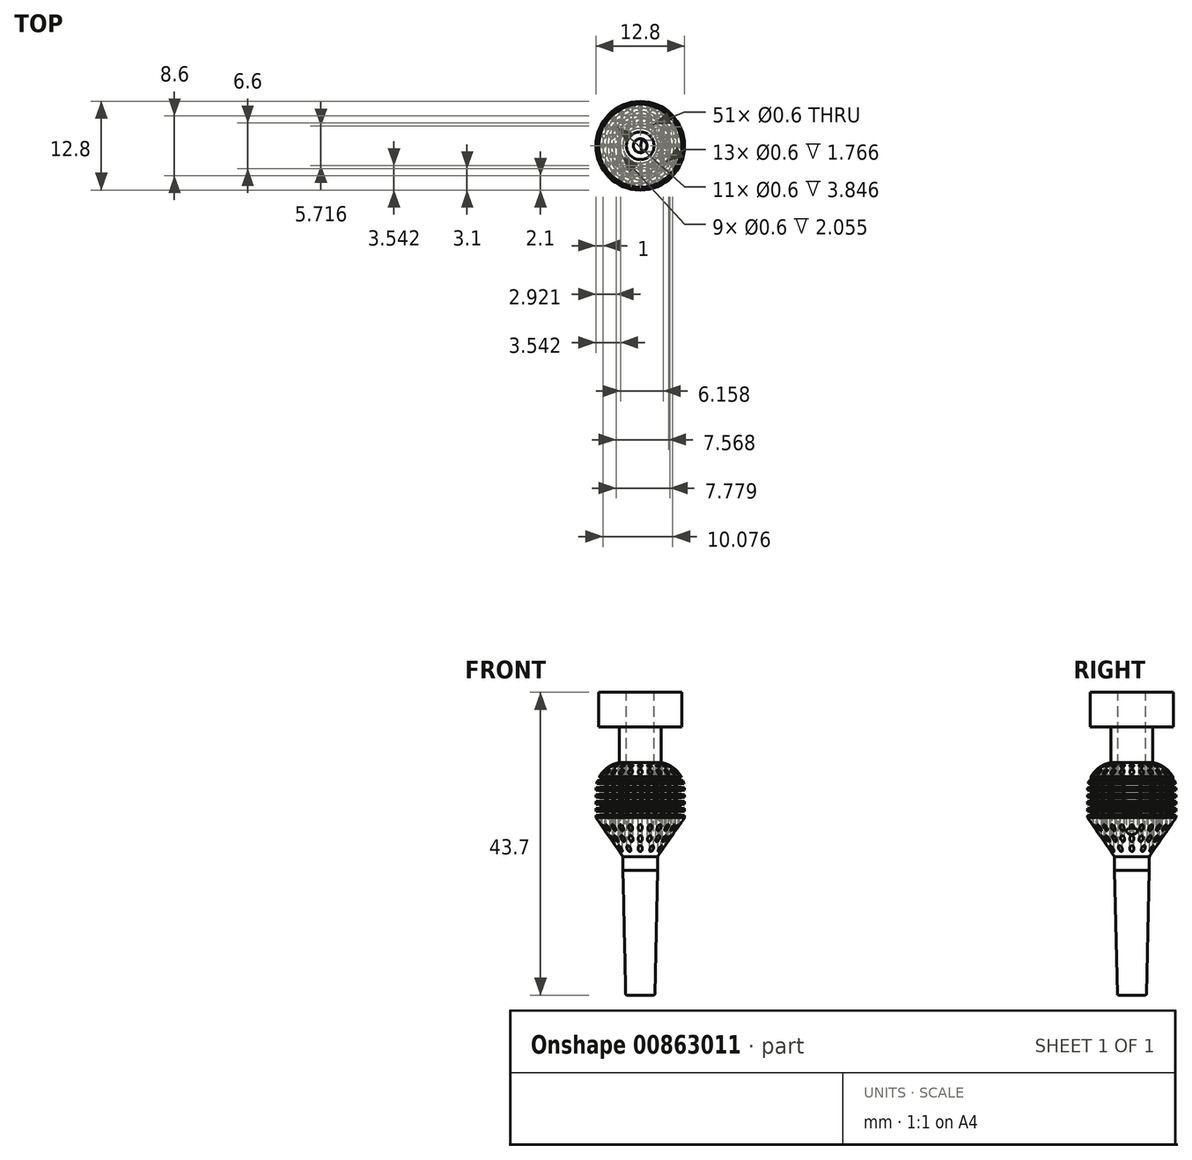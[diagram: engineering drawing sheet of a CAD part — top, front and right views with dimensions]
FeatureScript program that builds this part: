
annotation { "Feature Type Name" : "Feature", "Feature Type Description" : "" }
export const myFeature = defineFeature(function(context is Context, id is Id, definition is map)
    precondition{}
    {
        {
            var Q0;
            Q0=qCreatedBy(makeId("Front.planeOp"),FACE);
            var sketch = newSketch(context, id + "F0", { "sketchPlane" : qUnion([Q0])});
            skLineSegment(sketch, "E0", {"start": v(0, 0) * mm, "end": v(0, -20) * mm});
            skLineSegment(sketch, "E1", {"start": v(0, -20) * mm, "end": v(2.5, -20) * mm});
            skLineSegment(sketch, "E2", {"start": v(2.5, -20) * mm, "end": v(2.5, -0.32) * mm});
            skLineSegment(sketch, "E3", {"start": v(2.68, 0.26) * mm, "end": v(6.33, 5.48) * mm});
            skLineSegment(sketch, "E4", {"start": v(6.52, 6.05) * mm, "end": v(6.52, 9.73) * mm});
            skArc(sketch, "E5", {"start": v(6.52, 9.73) * mm, "mid": v(5.34, 12.57) * mm, "end": v(2.5, 13.73) * mm});
            skLineSegment(sketch, "E6", {"start": v(2.5, 13.73) * mm, "end": v(0, 13.72) * mm});
            skLineSegment(sketch, "E7", {"start": v(0, 0) * mm, "end": v(0, 13.72) * mm});
            skPoint(sketch, "E8.visualSharp", {"position": v(2.5, 0) * mm});
            skArc(sketch, "E8.filletArc", {"start": v(2.68, 0.26) * mm, "mid": v(2.55, -0.01) * mm, "end": v(2.5, -0.32) * mm});
            skPoint(sketch, "E9.visualSharp", {"position": v(6.52, 5.73) * mm});
            skArc(sketch, "E9.filletArc", {"start": v(6.33, 5.48) * mm, "mid": v(6.47, 5.75) * mm, "end": v(6.52, 6.05) * mm});
            skSolve(sketch);
        }
        {
            var Q0;
            Q0=makeQuery(id+"F0.imprint","IMPRINT",FACE,{"disambiguationData":[TD([[makeQuery(id+"F0.imprint","IMPRINT",EDGE,{"derivedFrom":sQuery(id+"F0.wireOp",EDGE,"E0")}),1.0]])]});
            var Q1;
            Q1=sQuery(id+"F0.wireOp",EDGE,"E7");
            revolve(context, id + "F1", {"surfaceOperationType" : NewSurfaceOperationType.NEW, "entities" : qUnion([Q0]), "axis" : qUnion([Q1]), "revolveType" : RevolveType.FULL});
        }
        {
            var Q0;
            Q0=qCreatedBy(makeId("Front.planeOp"),FACE);
            var sketch = newSketch(context, id + "F2", { "sketchPlane" : qUnion([Q0])});
            skLineSegment(sketch, "E10.bottom", {"start": v(2.5, 11.5) * mm, "end": v(7.5, 11.5) * mm});
            skLineSegment(sketch, "E10.top", {"start": v(2.5, 11) * mm, "end": v(7.5, 11) * mm});
            skLineSegment(sketch, "E10.left", {"start": v(2.5, 11.5) * mm, "end": v(2.5, 11) * mm});
            skLineSegment(sketch, "E10.right", {"start": v(7.5, 11.5) * mm, "end": v(7.5, 11) * mm});
            skLineSegment(sketch, "E11.0.1.0", {"start": v(2.5, 10) * mm, "end": v(7.5, 10) * mm});
            skLineSegment(sketch, "E11.0.1.1", {"start": v(2.5, 10.5) * mm, "end": v(7.5, 10.5) * mm});
            skLineSegment(sketch, "E11.0.1.2", {"start": v(2.5, 10.5) * mm, "end": v(2.5, 10) * mm});
            skLineSegment(sketch, "E11.0.1.3", {"start": v(7.5, 10.5) * mm, "end": v(7.5, 10) * mm});
            skLineSegment(sketch, "E11.0.2.0", {"start": v(2.5, 9) * mm, "end": v(7.5, 9) * mm});
            skLineSegment(sketch, "E11.0.2.1", {"start": v(2.5, 9.5) * mm, "end": v(7.5, 9.5) * mm});
            skLineSegment(sketch, "E11.0.2.2", {"start": v(2.5, 9.5) * mm, "end": v(2.5, 9) * mm});
            skLineSegment(sketch, "E11.0.2.3", {"start": v(7.5, 9.5) * mm, "end": v(7.5, 9) * mm});
            skLineSegment(sketch, "E11.0.3.0", {"start": v(2.5, 8) * mm, "end": v(7.5, 8) * mm});
            skLineSegment(sketch, "E11.0.3.1", {"start": v(2.5, 8.5) * mm, "end": v(7.5, 8.5) * mm});
            skLineSegment(sketch, "E11.0.3.2", {"start": v(2.5, 8.5) * mm, "end": v(2.5, 8) * mm});
            skLineSegment(sketch, "E11.0.3.3", {"start": v(7.5, 8.5) * mm, "end": v(7.5, 8) * mm});
            skLineSegment(sketch, "E11.direction1", {"start": v(2.5, 11) * mm, "end": v(27.5, 11) * mm, "construction": true});
            skLineSegment(sketch, "E11.direction2", {"start": v(2.5, 11) * mm, "end": v(2.5, 10) * mm, "construction": true});
            skLineSegment(sketch, "E12.0.0.4", {"start": v(2.5, 7) * mm, "end": v(7.5, 7) * mm});
            skLineSegment(sketch, "E12.3.0.4", {"start": v(2.5, 7.5) * mm, "end": v(7.5, 7.5) * mm});
            skLineSegment(sketch, "E12.6.0.4", {"start": v(2.5, 7.5) * mm, "end": v(2.5, 7) * mm});
            skLineSegment(sketch, "E12.9.0.4", {"start": v(7.5, 7.5) * mm, "end": v(7.5, 7) * mm});
            skLineSegment(sketch, "E13.0.0.5", {"start": v(2.5, 6) * mm, "end": v(7.5, 6) * mm});
            skLineSegment(sketch, "E13.3.0.5", {"start": v(2.5, 6.5) * mm, "end": v(7.5, 6.5) * mm});
            skLineSegment(sketch, "E13.6.0.5", {"start": v(2.5, 6.5) * mm, "end": v(2.5, 6) * mm});
            skLineSegment(sketch, "E13.9.0.5", {"start": v(7.5, 6.5) * mm, "end": v(7.5, 6) * mm});
            skSolve(sketch);
        }
        {
            var Q0;
            Q0=qCreatedBy(makeId("Front.planeOp"),FACE);
            var sketch = newSketch(context, id + "F3", { "sketchPlane" : qUnion([Q0])});
            skLineSegment(sketch, "E14", {"start": v(0, 35.11) * mm, "end": v(0, -39.83) * mm, "construction": true});
            skSolve(sketch);
        }
        {
            var Q0;
            Q0=qSketchRegion(id+"F2",true);
            var Q1;
            Q1=sQuery(id+"F3.wireOp",EDGE,"E14");
            var Q2;
            Q2=qConstructionFilter(qBodyType(qCreatedBy(id+"F2",EDGE),BodyType.WIRE),ConstructionObject.NO);
            var Q3;
            Q3=sQuery(id+"F3.wireOp",EDGE,"E14");
            revolve(context, id + "F4", {"operationType" : NewBodyOperationType.REMOVE, "surfaceOperationType" : NewSurfaceOperationType.NEW, "entities" : qUnion([Q0]), "surfaceEntities" : qUnion([Q1, Q2]), "axis" : qUnion([Q3]), "revolveType" : RevolveType.FULL, "oppositeDirection" : true});
        }
        {
            var Q0;
            Q0=qCreatedBy(makeId("Top.planeOp"),FACE);
            cPlane(context, id + "F5", {"entities" : qUnion([Q0]), "cplaneType" : CPlaneType.OFFSET, "offset" : 13.7 * mm, "width" : 150 * mm, "height" : 150 * mm});
        }
        {
            var Q0;
            Q0=qCreatedBy(id+"F5.planeOp",FACE);
            var sketch = newSketch(context, id + "F6", { "sketchPlane" : qUnion([Q0])});
            skCircle(sketch, "E15", {"center": v(0, 3.3) * mm, "radius": 0.3 * mm});
            skCircle(sketch, "E16.1.0", {"center": v(-1.65, 2.86) * mm, "radius": 0.3 * mm});
            skCircle(sketch, "E16.2.0", {"center": v(-2.86, 1.65) * mm, "radius": 0.3 * mm});
            skCircle(sketch, "E16.3.0", {"center": v(-3.3, 0) * mm, "radius": 0.3 * mm});
            skCircle(sketch, "E16.4.0", {"center": v(-2.86, -1.65) * mm, "radius": 0.3 * mm});
            skCircle(sketch, "E16.5.0", {"center": v(-1.65, -2.86) * mm, "radius": 0.3 * mm});
            skCircle(sketch, "E16.6.0", {"center": v(0, -3.3) * mm, "radius": 0.3 * mm});
            skCircle(sketch, "E16.7.0", {"center": v(1.65, -2.86) * mm, "radius": 0.3 * mm});
            skCircle(sketch, "E16.8.0", {"center": v(2.86, -1.65) * mm, "radius": 0.3 * mm});
            skCircle(sketch, "E16.9.0", {"center": v(3.3, 0) * mm, "radius": 0.3 * mm});
            skPoint(sketch, "E16.center", {"position": v(0, 0) * mm});
            skCircle(sketch, "E17", {"center": v(0, 4.3) * mm, "radius": 0.3 * mm});
            skCircle(sketch, "E18.1.0", {"center": v(-1.33, 4.09) * mm, "radius": 0.3 * mm});
            skCircle(sketch, "E18.2.0", {"center": v(-2.53, 3.48) * mm, "radius": 0.3 * mm});
            skCircle(sketch, "E18.3.0", {"center": v(-3.48, 2.53) * mm, "radius": 0.3 * mm});
            skCircle(sketch, "E18.4.0", {"center": v(-4.09, 1.33) * mm, "radius": 0.3 * mm});
            skCircle(sketch, "E18.5.0", {"center": v(-4.3, 0) * mm, "radius": 0.3 * mm});
            skCircle(sketch, "E18.6.0", {"center": v(-4.09, -1.33) * mm, "radius": 0.3 * mm});
            skCircle(sketch, "E18.7.0", {"center": v(-3.48, -2.53) * mm, "radius": 0.3 * mm});
            skCircle(sketch, "E18.8.0", {"center": v(-2.53, -3.48) * mm, "radius": 0.3 * mm});
            skCircle(sketch, "E18.9.0", {"center": v(-1.33, -4.09) * mm, "radius": 0.3 * mm});
            skCircle(sketch, "E18.10.0", {"center": v(0, -4.3) * mm, "radius": 0.3 * mm});
            skCircle(sketch, "E18.11.0", {"center": v(1.33, -4.09) * mm, "radius": 0.3 * mm});
            skCircle(sketch, "E18.12.0", {"center": v(2.53, -3.48) * mm, "radius": 0.3 * mm});
            skCircle(sketch, "E18.13.0", {"center": v(3.48, -2.53) * mm, "radius": 0.3 * mm});
            skCircle(sketch, "E18.14.0", {"center": v(4.09, -1.33) * mm, "radius": 0.3 * mm});
            skCircle(sketch, "E18.15.0", {"center": v(4.3, 0) * mm, "radius": 0.3 * mm});
            skCircle(sketch, "E19", {"center": v(0, 5.4) * mm, "radius": 0.3 * mm});
            skCircle(sketch, "E20.1.0", {"center": v(-1.4, 5.22) * mm, "radius": 0.3 * mm});
            skCircle(sketch, "E20.2.0", {"center": v(-2.7, 4.68) * mm, "radius": 0.3 * mm});
            skCircle(sketch, "E20.3.0", {"center": v(-3.82, 3.82) * mm, "radius": 0.3 * mm});
            skCircle(sketch, "E20.4.0", {"center": v(-4.68, 2.7) * mm, "radius": 0.3 * mm});
            skCircle(sketch, "E20.5.0", {"center": v(-5.22, 1.4) * mm, "radius": 0.3 * mm});
            skCircle(sketch, "E20.6.0", {"center": v(-5.4, 0) * mm, "radius": 0.3 * mm});
            skCircle(sketch, "E20.7.0", {"center": v(-5.22, -1.4) * mm, "radius": 0.3 * mm});
            skCircle(sketch, "E20.8.0", {"center": v(-4.68, -2.7) * mm, "radius": 0.3 * mm});
            skCircle(sketch, "E20.9.0", {"center": v(-3.82, -3.82) * mm, "radius": 0.3 * mm});
            skCircle(sketch, "E20.10.0", {"center": v(-2.7, -4.68) * mm, "radius": 0.3 * mm});
            skCircle(sketch, "E20.11.0", {"center": v(-1.4, -5.22) * mm, "radius": 0.3 * mm});
            skCircle(sketch, "E20.12.0", {"center": v(0, -5.4) * mm, "radius": 0.3 * mm});
            skCircle(sketch, "E20.13.0", {"center": v(1.4, -5.22) * mm, "radius": 0.3 * mm});
            skCircle(sketch, "E20.14.0", {"center": v(2.7, -4.68) * mm, "radius": 0.3 * mm});
            skCircle(sketch, "E20.15.0", {"center": v(3.82, -3.82) * mm, "radius": 0.3 * mm});
            skCircle(sketch, "E20.16.0", {"center": v(4.68, -2.7) * mm, "radius": 0.3 * mm});
            skCircle(sketch, "E20.17.0", {"center": v(5.22, -1.4) * mm, "radius": 0.3 * mm});
            skCircle(sketch, "E20.18.0", {"center": v(5.4, 0) * mm, "radius": 0.3 * mm});
            skCircle(sketch, "E20.19.0", {"center": v(5.22, 1.4) * mm, "radius": 0.3 * mm});
            skCircle(sketch, "E21.1.10.0", {"center": v(2.86, 1.65) * mm, "radius": 0.3 * mm});
            skCircle(sketch, "E21.1.11.0", {"center": v(1.65, 2.86) * mm, "radius": 0.3 * mm});
            skCircle(sketch, "E22.1.16.0", {"center": v(4.09, 1.33) * mm, "radius": 0.3 * mm});
            skCircle(sketch, "E22.1.17.0", {"center": v(3.48, 2.53) * mm, "radius": 0.3 * mm});
            skCircle(sketch, "E22.1.18.0", {"center": v(2.53, 3.48) * mm, "radius": 0.3 * mm});
            skCircle(sketch, "E22.1.19.0", {"center": v(1.33, 4.09) * mm, "radius": 0.3 * mm});
            skCircle(sketch, "E23.1.20.0", {"center": v(4.68, 2.7) * mm, "radius": 0.3 * mm});
            skCircle(sketch, "E23.1.21.0", {"center": v(3.82, 3.82) * mm, "radius": 0.3 * mm});
            skCircle(sketch, "E23.1.22.0", {"center": v(2.7, 4.68) * mm, "radius": 0.3 * mm});
            skCircle(sketch, "E23.1.23.0", {"center": v(1.4, 5.22) * mm, "radius": 0.3 * mm});
            skSolve(sketch);
        }
        {
            var Q0;
            Q0=qSketchRegion(id+"F6",true);
            extrude(context, id + "F7", {"entities" : qUnion([Q0]), "operationType" : NewBodyOperationType.REMOVE, "oppositeDirection" : true, "depth" : 16.5 * mm, "offsetDistance" : 25 * mm});
        }
        {
            var Q0;
            Q0=qCreatedBy(makeId("Front.planeOp"),FACE);
            cPlane(context, id + "F8", {"entities" : qUnion([Q0]), "cplaneType" : CPlaneType.OFFSET, "offset" : 7 * mm, "width" : 150 * mm, "height" : 150 * mm});
        }
        {
            var Q0;
            Q0=qCreatedBy(id+"F8.planeOp",FACE);
            var sketch = newSketch(context, id + "F9", { "sketchPlane" : qUnion([Q0])});
            skLineSegment(sketch, "E24.bottom", {"start": v(-4.75, 11.8) * mm, "end": v(-5, 11.8) * mm});
            skLineSegment(sketch, "E24.top", {"start": v(-4.75, 5.8) * mm, "end": v(-5, 5.8) * mm});
            skLineSegment(sketch, "E24.left", {"start": v(-4.75, 11.8) * mm, "end": v(-4.75, 5.8) * mm});
            skLineSegment(sketch, "E24.right", {"start": v(-5, 11.8) * mm, "end": v(-5, 5.8) * mm});
            skLineSegment(sketch, "E25.1.0.0", {"start": v(-4, 11.8) * mm, "end": v(-4, 5.8) * mm});
            skLineSegment(sketch, "E25.1.0.1", {"start": v(-3.75, 11.8) * mm, "end": v(-3.75, 5.8) * mm});
            skLineSegment(sketch, "E25.1.0.2", {"start": v(-3.75, 5.8) * mm, "end": v(-4, 5.8) * mm});
            skLineSegment(sketch, "E25.1.0.3", {"start": v(-3.75, 11.8) * mm, "end": v(-4, 11.8) * mm});
            skLineSegment(sketch, "E25.2.0.0", {"start": v(-3, 11.8) * mm, "end": v(-3, 5.8) * mm});
            skLineSegment(sketch, "E25.2.0.1", {"start": v(-2.75, 11.8) * mm, "end": v(-2.75, 5.8) * mm});
            skLineSegment(sketch, "E25.2.0.2", {"start": v(-2.75, 5.8) * mm, "end": v(-3, 5.8) * mm});
            skLineSegment(sketch, "E25.2.0.3", {"start": v(-2.75, 11.8) * mm, "end": v(-3, 11.8) * mm});
            skLineSegment(sketch, "E25.3.0.0", {"start": v(-2, 11.8) * mm, "end": v(-2, 5.8) * mm});
            skLineSegment(sketch, "E25.3.0.1", {"start": v(-1.75, 11.8) * mm, "end": v(-1.75, 5.8) * mm});
            skLineSegment(sketch, "E25.3.0.2", {"start": v(-1.75, 5.8) * mm, "end": v(-2, 5.8) * mm});
            skLineSegment(sketch, "E25.3.0.3", {"start": v(-1.75, 11.8) * mm, "end": v(-2, 11.8) * mm});
            skLineSegment(sketch, "E25.4.0.0", {"start": v(-1, 11.8) * mm, "end": v(-1, 5.8) * mm});
            skLineSegment(sketch, "E25.4.0.1", {"start": v(-0.75, 11.8) * mm, "end": v(-0.75, 5.8) * mm});
            skLineSegment(sketch, "E25.4.0.2", {"start": v(-0.75, 5.8) * mm, "end": v(-1, 5.8) * mm});
            skLineSegment(sketch, "E25.4.0.3", {"start": v(-0.75, 11.8) * mm, "end": v(-1, 11.8) * mm});
            skLineSegment(sketch, "E25.5.0.0", {"start": v(0, 11.8) * mm, "end": v(0, 5.8) * mm});
            skLineSegment(sketch, "E25.5.0.1", {"start": v(0.25, 11.8) * mm, "end": v(0.25, 5.8) * mm});
            skLineSegment(sketch, "E25.5.0.2", {"start": v(0.25, 5.8) * mm, "end": v(0, 5.8) * mm});
            skLineSegment(sketch, "E25.5.0.3", {"start": v(0.25, 11.8) * mm, "end": v(0, 11.8) * mm});
            skLineSegment(sketch, "E25.6.0.0", {"start": v(1, 11.8) * mm, "end": v(1, 5.8) * mm});
            skLineSegment(sketch, "E25.6.0.1", {"start": v(1.25, 11.8) * mm, "end": v(1.25, 5.8) * mm});
            skLineSegment(sketch, "E25.6.0.2", {"start": v(1.25, 5.8) * mm, "end": v(1, 5.8) * mm});
            skLineSegment(sketch, "E25.6.0.3", {"start": v(1.25, 11.8) * mm, "end": v(1, 11.8) * mm});
            skLineSegment(sketch, "E25.7.0.0", {"start": v(2, 11.8) * mm, "end": v(2, 5.8) * mm});
            skLineSegment(sketch, "E25.7.0.1", {"start": v(2.25, 11.8) * mm, "end": v(2.25, 5.8) * mm});
            skLineSegment(sketch, "E25.7.0.2", {"start": v(2.25, 5.8) * mm, "end": v(2, 5.8) * mm});
            skLineSegment(sketch, "E25.7.0.3", {"start": v(2.25, 11.8) * mm, "end": v(2, 11.8) * mm});
            skLineSegment(sketch, "E25.8.0.0", {"start": v(3, 11.8) * mm, "end": v(3, 5.8) * mm});
            skLineSegment(sketch, "E25.8.0.1", {"start": v(3.25, 11.8) * mm, "end": v(3.25, 5.8) * mm});
            skLineSegment(sketch, "E25.8.0.2", {"start": v(3.25, 5.8) * mm, "end": v(3, 5.8) * mm});
            skLineSegment(sketch, "E25.8.0.3", {"start": v(3.25, 11.8) * mm, "end": v(3, 11.8) * mm});
            skLineSegment(sketch, "E25.9.0.0", {"start": v(4, 11.8) * mm, "end": v(4, 5.8) * mm});
            skLineSegment(sketch, "E25.9.0.1", {"start": v(4.25, 11.8) * mm, "end": v(4.25, 5.8) * mm});
            skLineSegment(sketch, "E25.9.0.2", {"start": v(4.25, 5.8) * mm, "end": v(4, 5.8) * mm});
            skLineSegment(sketch, "E25.9.0.3", {"start": v(4.25, 11.8) * mm, "end": v(4, 11.8) * mm});
            skLineSegment(sketch, "E25.10.0.0", {"start": v(5, 11.8) * mm, "end": v(5, 5.8) * mm});
            skLineSegment(sketch, "E25.10.0.1", {"start": v(5.25, 11.8) * mm, "end": v(5.25, 5.8) * mm});
            skLineSegment(sketch, "E25.10.0.2", {"start": v(5.25, 5.8) * mm, "end": v(5, 5.8) * mm});
            skLineSegment(sketch, "E25.10.0.3", {"start": v(5.25, 11.8) * mm, "end": v(5, 11.8) * mm});
            skLineSegment(sketch, "E25.direction1", {"start": v(-5, 5.8) * mm, "end": v(-4, 5.8) * mm, "construction": true});
            skLineSegment(sketch, "E25.direction2", {"start": v(-5, 5.8) * mm, "end": v(-5, 3.8) * mm, "construction": true});
            skSolve(sketch);
        }
        {
            var Q0;
            Q0=qSketchRegion(id+"F9",true);
            extrude(context, id + "F10", {"entities" : qUnion([Q0]), "operationType" : NewBodyOperationType.ADD, "oppositeDirection" : true, "depth" : 14.3 * mm, "offsetDistance" : 25 * mm});
        }
        {
            var Q0;
            Q0=qCreatedBy(makeId("Right.planeOp"),FACE);
            var sketch = newSketch(context, id + "F11", { "sketchPlane" : qUnion([Q0])});
            skLineSegment(sketch, "E26", {"start": v(-2.5, 0) * mm, "end": v(-6.4, 5.6) * mm});
            skLineSegment(sketch, "E27", {"start": v(-6.4, 5.6) * mm, "end": v(-6.4, 9.6) * mm});
            skArc(sketch, "E28", {"start": v(-2.4, 13.6) * mm, "mid": v(-5.23, 12.43) * mm, "end": v(-6.4, 9.6) * mm});
            skLineSegment(sketch, "E29", {"start": v(-2.4, 13.6) * mm, "end": v(-2.4, 16) * mm});
            skLineSegment(sketch, "E30", {"start": v(-2.4, 16) * mm, "end": v(-14.4, 16) * mm});
            skLineSegment(sketch, "E31", {"start": v(-14.4, 16) * mm, "end": v(-14.5, 0) * mm});
            skLineSegment(sketch, "E32", {"start": v(-14.5, 0) * mm, "end": v(-2.5, 0) * mm});
            skSolve(sketch);
        }
        {
            var Q0;
            Q0=qCreatedBy(makeId("Right.planeOp"),FACE);
            var sketch = newSketch(context, id + "F12", { "sketchPlane" : qUnion([Q0])});
            skLineSegment(sketch, "E33", {"start": v(0, -8.71) * mm, "end": v(0, 18.1) * mm, "construction": true});
            skSolve(sketch);
        }
        {
            var Q0;
            Q0=makeQuery(id+"F11.imprint","IMPRINT",FACE,{"disambiguationData":[TD([[makeQuery(id+"F11.imprint","IMPRINT",EDGE,{"derivedFrom":sQuery(id+"F11.wireOp",EDGE,"E26")}),1.0]])]});
            var Q1;
            Q1=sQuery(id+"F12.wireOp",EDGE,"E33");
            var Q2;
            Q2=sQuery(id+"F12.wireOp",EDGE,"E33");
            revolve(context, id + "F13", {"operationType" : NewBodyOperationType.REMOVE, "surfaceOperationType" : NewSurfaceOperationType.NEW, "entities" : qUnion([Q0]), "surfaceEntities" : qUnion([Q1]), "axis" : qUnion([Q2]), "revolveType" : RevolveType.FULL, "oppositeDirection" : true});
        }
        {
            var Q0;
            Q0=qCreatedBy(id+"F5.planeOp",FACE);
            var sketch = newSketch(context, id + "F14", { "sketchPlane" : qUnion([Q0])});
            skCircle(sketch, "E34", {"center": v(0, 0) * mm, "radius": 3 * mm});
            skSolve(sketch);
        }
        {
            var Q0;
            Q0=qSketchRegion(id+"F14",true);
            extrude(context, id + "F15", {"entities" : qUnion([Q0]), "operationType" : NewBodyOperationType.ADD, "depth" : 10 * mm, "offsetDistance" : 25 * mm, "hasSecondDirection" : true, "secondDirectionOppositeDirection" : true, "secondDirectionDepth" : 1 * mm});
        }
        {
            var Q0;
            Q0=qCreatedBy(makeId("Right.planeOp"),FACE);
            var sketch = newSketch(context, id + "F16", { "sketchPlane" : qUnion([Q0])});
            skLineSegment(sketch, "E35.bottom", {"start": v(-6.4, 5.95) * mm, "end": v(-5.9, 5.95) * mm});
            skLineSegment(sketch, "E35.top", {"start": v(-6.4, 6.55) * mm, "end": v(-5.9, 6.55) * mm});
            skLineSegment(sketch, "E35.left", {"start": v(-6.4, 5.95) * mm, "end": v(-6.4, 6.55) * mm});
            skLineSegment(sketch, "E35.right", {"start": v(-5.9, 5.95) * mm, "end": v(-5.9, 6.55) * mm});
            skLineSegment(sketch, "E36.0.1.0", {"start": v(-6.4, 7.55) * mm, "end": v(-5.9, 7.55) * mm});
            skLineSegment(sketch, "E36.0.1.1", {"start": v(-5.9, 6.95) * mm, "end": v(-5.9, 7.55) * mm});
            skLineSegment(sketch, "E36.0.1.2", {"start": v(-6.4, 6.95) * mm, "end": v(-6.4, 7.55) * mm});
            skLineSegment(sketch, "E36.0.1.3", {"start": v(-6.4, 6.95) * mm, "end": v(-5.9, 6.95) * mm});
            skLineSegment(sketch, "E36.0.2.0", {"start": v(-6.4, 8.55) * mm, "end": v(-5.9, 8.55) * mm});
            skLineSegment(sketch, "E36.0.2.1", {"start": v(-5.9, 7.95) * mm, "end": v(-5.9, 8.55) * mm});
            skLineSegment(sketch, "E36.0.2.2", {"start": v(-6.4, 7.95) * mm, "end": v(-6.4, 8.55) * mm});
            skLineSegment(sketch, "E36.0.2.3", {"start": v(-6.4, 7.95) * mm, "end": v(-5.9, 7.95) * mm});
            skLineSegment(sketch, "E36.0.3.0", {"start": v(-6.4, 9.55) * mm, "end": v(-5.9, 9.55) * mm});
            skLineSegment(sketch, "E36.0.3.1", {"start": v(-5.9, 8.95) * mm, "end": v(-5.9, 9.55) * mm});
            skLineSegment(sketch, "E36.0.3.2", {"start": v(-6.4, 8.95) * mm, "end": v(-6.4, 9.55) * mm});
            skLineSegment(sketch, "E36.0.3.3", {"start": v(-6.4, 8.95) * mm, "end": v(-5.9, 8.95) * mm});
            skLineSegment(sketch, "E36.0.4.0", {"start": v(-6.4, 10.55) * mm, "end": v(-5.9, 10.55) * mm});
            skLineSegment(sketch, "E36.0.4.1", {"start": v(-5.9, 9.95) * mm, "end": v(-5.9, 10.55) * mm});
            skLineSegment(sketch, "E36.0.4.2", {"start": v(-6.4, 9.95) * mm, "end": v(-6.4, 10.55) * mm});
            skLineSegment(sketch, "E36.0.4.3", {"start": v(-6.4, 9.95) * mm, "end": v(-5.9, 9.95) * mm});
            skLineSegment(sketch, "E36.0.5.0", {"start": v(-6.4, 11.55) * mm, "end": v(-5.9, 11.55) * mm});
            skLineSegment(sketch, "E36.0.5.1", {"start": v(-5.9, 10.95) * mm, "end": v(-5.9, 11.55) * mm});
            skLineSegment(sketch, "E36.0.5.2", {"start": v(-6.4, 10.95) * mm, "end": v(-6.4, 11.55) * mm});
            skLineSegment(sketch, "E36.0.5.3", {"start": v(-6.4, 10.95) * mm, "end": v(-5.9, 10.95) * mm});
            skLineSegment(sketch, "E36.1.0.0", {"start": v(-5.4, 6.55) * mm, "end": v(-4.9, 6.55) * mm});
            skLineSegment(sketch, "E36.1.0.1", {"start": v(-4.9, 5.95) * mm, "end": v(-4.9, 6.55) * mm});
            skLineSegment(sketch, "E36.1.0.2", {"start": v(-5.4, 5.95) * mm, "end": v(-5.4, 6.55) * mm});
            skLineSegment(sketch, "E36.1.0.3", {"start": v(-5.4, 5.95) * mm, "end": v(-4.9, 5.95) * mm});
            skLineSegment(sketch, "E36.1.1.0", {"start": v(-5.4, 7.55) * mm, "end": v(-4.9, 7.55) * mm});
            skLineSegment(sketch, "E36.1.1.1", {"start": v(-4.9, 6.95) * mm, "end": v(-4.9, 7.55) * mm});
            skLineSegment(sketch, "E36.1.1.2", {"start": v(-5.4, 6.95) * mm, "end": v(-5.4, 7.55) * mm});
            skLineSegment(sketch, "E36.1.1.3", {"start": v(-5.4, 6.95) * mm, "end": v(-4.9, 6.95) * mm});
            skLineSegment(sketch, "E36.1.2.0", {"start": v(-5.4, 8.55) * mm, "end": v(-4.9, 8.55) * mm});
            skLineSegment(sketch, "E36.1.2.1", {"start": v(-4.9, 7.95) * mm, "end": v(-4.9, 8.55) * mm});
            skLineSegment(sketch, "E36.1.2.2", {"start": v(-5.4, 7.95) * mm, "end": v(-5.4, 8.55) * mm});
            skLineSegment(sketch, "E36.1.2.3", {"start": v(-5.4, 7.95) * mm, "end": v(-4.9, 7.95) * mm});
            skLineSegment(sketch, "E36.1.3.0", {"start": v(-5.4, 9.55) * mm, "end": v(-4.9, 9.55) * mm});
            skLineSegment(sketch, "E36.1.3.1", {"start": v(-4.9, 8.95) * mm, "end": v(-4.9, 9.55) * mm});
            skLineSegment(sketch, "E36.1.3.2", {"start": v(-5.4, 8.95) * mm, "end": v(-5.4, 9.55) * mm});
            skLineSegment(sketch, "E36.1.3.3", {"start": v(-5.4, 8.95) * mm, "end": v(-4.9, 8.95) * mm});
            skLineSegment(sketch, "E36.1.4.0", {"start": v(-5.4, 10.55) * mm, "end": v(-4.9, 10.55) * mm});
            skLineSegment(sketch, "E36.1.4.1", {"start": v(-4.9, 9.95) * mm, "end": v(-4.9, 10.55) * mm});
            skLineSegment(sketch, "E36.1.4.2", {"start": v(-5.4, 9.95) * mm, "end": v(-5.4, 10.55) * mm});
            skLineSegment(sketch, "E36.1.4.3", {"start": v(-5.4, 9.95) * mm, "end": v(-4.9, 9.95) * mm});
            skLineSegment(sketch, "E36.1.5.0", {"start": v(-5.4, 11.55) * mm, "end": v(-4.9, 11.55) * mm});
            skLineSegment(sketch, "E36.1.5.1", {"start": v(-4.9, 10.95) * mm, "end": v(-4.9, 11.55) * mm});
            skLineSegment(sketch, "E36.1.5.2", {"start": v(-5.4, 10.95) * mm, "end": v(-5.4, 11.55) * mm});
            skLineSegment(sketch, "E36.1.5.3", {"start": v(-5.4, 10.95) * mm, "end": v(-4.9, 10.95) * mm});
            skLineSegment(sketch, "E36.2.0.0", {"start": v(-4.4, 6.55) * mm, "end": v(-3.9, 6.55) * mm});
            skLineSegment(sketch, "E36.2.0.1", {"start": v(-3.9, 5.95) * mm, "end": v(-3.9, 6.55) * mm});
            skLineSegment(sketch, "E36.2.0.2", {"start": v(-4.4, 5.95) * mm, "end": v(-4.4, 6.55) * mm});
            skLineSegment(sketch, "E36.2.0.3", {"start": v(-4.4, 5.95) * mm, "end": v(-3.9, 5.95) * mm});
            skLineSegment(sketch, "E36.2.1.0", {"start": v(-4.4, 7.55) * mm, "end": v(-3.9, 7.55) * mm});
            skLineSegment(sketch, "E36.2.1.1", {"start": v(-3.9, 6.95) * mm, "end": v(-3.9, 7.55) * mm});
            skLineSegment(sketch, "E36.2.1.2", {"start": v(-4.4, 6.95) * mm, "end": v(-4.4, 7.55) * mm});
            skLineSegment(sketch, "E36.2.1.3", {"start": v(-4.4, 6.95) * mm, "end": v(-3.9, 6.95) * mm});
            skLineSegment(sketch, "E36.2.2.0", {"start": v(-4.4, 8.55) * mm, "end": v(-3.9, 8.55) * mm});
            skLineSegment(sketch, "E36.2.2.1", {"start": v(-3.9, 7.95) * mm, "end": v(-3.9, 8.55) * mm});
            skLineSegment(sketch, "E36.2.2.2", {"start": v(-4.4, 7.95) * mm, "end": v(-4.4, 8.55) * mm});
            skLineSegment(sketch, "E36.2.2.3", {"start": v(-4.4, 7.95) * mm, "end": v(-3.9, 7.95) * mm});
            skLineSegment(sketch, "E36.2.3.0", {"start": v(-4.4, 9.55) * mm, "end": v(-3.9, 9.55) * mm});
            skLineSegment(sketch, "E36.2.3.1", {"start": v(-3.9, 8.95) * mm, "end": v(-3.9, 9.55) * mm});
            skLineSegment(sketch, "E36.2.3.2", {"start": v(-4.4, 8.95) * mm, "end": v(-4.4, 9.55) * mm});
            skLineSegment(sketch, "E36.2.3.3", {"start": v(-4.4, 8.95) * mm, "end": v(-3.9, 8.95) * mm});
            skLineSegment(sketch, "E36.2.4.0", {"start": v(-4.4, 10.55) * mm, "end": v(-3.9, 10.55) * mm});
            skLineSegment(sketch, "E36.2.4.1", {"start": v(-3.9, 9.95) * mm, "end": v(-3.9, 10.55) * mm});
            skLineSegment(sketch, "E36.2.4.2", {"start": v(-4.4, 9.95) * mm, "end": v(-4.4, 10.55) * mm});
            skLineSegment(sketch, "E36.2.4.3", {"start": v(-4.4, 9.95) * mm, "end": v(-3.9, 9.95) * mm});
            skLineSegment(sketch, "E36.2.5.0", {"start": v(-4.4, 11.55) * mm, "end": v(-3.9, 11.55) * mm});
            skLineSegment(sketch, "E36.2.5.1", {"start": v(-3.9, 10.95) * mm, "end": v(-3.9, 11.55) * mm});
            skLineSegment(sketch, "E36.2.5.2", {"start": v(-4.4, 10.95) * mm, "end": v(-4.4, 11.55) * mm});
            skLineSegment(sketch, "E36.2.5.3", {"start": v(-4.4, 10.95) * mm, "end": v(-3.9, 10.95) * mm});
            skLineSegment(sketch, "E36.direction1", {"start": v(-6.4, 5.95) * mm, "end": v(-5.4, 5.95) * mm, "construction": true});
            skLineSegment(sketch, "E36.direction2", {"start": v(-6.4, 5.95) * mm, "end": v(-6.4, 6.95) * mm, "construction": true});
            skSolve(sketch);
        }
        {
            var Q0;
            Q0=qCreatedBy(makeId("Right.planeOp"),FACE);
            var sketch = newSketch(context, id + "F17", { "sketchPlane" : qUnion([Q0])});
            skLineSegment(sketch, "E37", {"start": v(0, 46.38) * mm, "end": v(0, -33.28) * mm, "construction": true});
            skSolve(sketch);
        }
        {
            var Q0;
            Q0 = qSketchRegion(id + "F16", true);
            var Q1;
            Q1 = qConstructionFilter(qBodyType(qCreatedBy(id + "F16" ,EDGE), BodyType.WIRE), ConstructionObject.NO);
            var Q2;
            Q2=sQuery(id+"F17.wireOp",EDGE,"E37");
            revolve(context, id + "F18", {"operationType" : NewBodyOperationType.REMOVE, "surfaceOperationType" : NewSurfaceOperationType.NEW, "entities" : qUnion([Q0]), "surfaceEntities" : qUnion([Q1]), "axis" : qUnion([Q2]), "revolveType" : RevolveType.FULL, "oppositeDirection" : true});
        }
        {
            var Q0;
            Q0=makeQuery(id+"F15.opExtrude","CAP_FACE",FACE,{"disambiguationData":[OSD([sQuery(id+"F14.wireOp",EDGE,"E34")])],"isStart":false});
            var sketch = newSketch(context, id + "F19", { "sketchPlane" : qUnion([Q0])});
            skCircle(sketch, "E38", {"center": v(0, 0) * mm, "radius": 2 * mm});
            skSolve(sketch);
        }
        {
            var Q0;
            Q0=makeQuery(id+"F19.imprint","IMPRINT",FACE,{"disambiguationData":[TD([[makeQuery(id+"F19.imprint","IMPRINT",EDGE,{"derivedFrom":sQuery(id+"F19.wireOp",EDGE,"E38")}),1.0]])]});
            var Q1;
            Q1=sQuery(id+"F19.wireOp",EDGE,"E38");
            extrude(context, id + "F20", {"entities" : qUnion([Q0]), "operationType" : NewBodyOperationType.REMOVE, "surfaceEntities" : qUnion([Q1]), "oppositeDirection" : true, "depth" : 15 * mm, "offsetDistance" : 25 * mm});
        }
        {
            var Q0;
            Q0=qCreatedBy(makeId("Front.planeOp"),FACE);
            var sketch = newSketch(context, id + "F21", { "sketchPlane" : qUnion([Q0])});
            skLineSegment(sketch, "E39", {"start": v(0, 8.7) * mm, "end": v(5.5, 3.2) * mm});
            skSolve(sketch);
        }
        {
            var Q0;
            Q0=qCreatedBy(makeId("Right.planeOp"),FACE);
            cPlane(context, id + "F22", {"entities" : qUnion([Q0]), "cplaneType" : CPlaneType.OFFSET, "offset" : 5.5 * mm, "width" : 150 * mm, "height" : 150 * mm});
        }
        {
            var Q0;
            Q0=qCreatedBy(id+"F22.planeOp",FACE);
            var sketch = newSketch(context, id + "F23", { "sketchPlane" : qUnion([Q0])});
            skCircle(sketch, "E40", {"center": v(0, 3.2) * mm, "radius": 1 * mm});
            skSolve(sketch);
        }
        {
            var Q0;
            Q0=makeQuery(id+"F23.imprint","IMPRINT",FACE,{"disambiguationData":[TD([[makeQuery(id+"F23.imprint","IMPRINT",EDGE,{"derivedFrom":sQuery(id+"F23.wireOp",EDGE,"E40")}),1.0]])]});
            var Q1;
            Q1=sQuery(id+"F21.wireOp",EDGE,"E39");
            sweep(context, id + "F24", {"operationType" : NewBodyOperationType.REMOVE, "profiles" : qUnion([Q0]), "path" : qUnion([Q1])});
        }
        {
            var Q0;
            Q0=qCreatedBy(makeId("Front.planeOp"),FACE);
            var sketch = newSketch(context, id + "F25", { "sketchPlane" : qUnion([Q0])});
            skLineSegment(sketch, "E41", {"start": v(0, 8.7) * mm, "end": v(5.5, 3.2) * mm});
            skSolve(sketch);
        }
        {
            var Q0;
            Q0=qCreatedBy(id+"F22.planeOp",FACE);
            var sketch = newSketch(context, id + "F26", { "sketchPlane" : qUnion([Q0])});
            skCircle(sketch, "E42", {"center": v(0, 3.2) * mm, "radius": 1 * mm});
            skCircle(sketch, "E43", {"center": v(0, 3.2) * mm, "radius": 0.8 * mm});
            skSolve(sketch);
        }
        {
            var Q0;
            Q0 = qSketchRegion(id + "F26", true);
            var Q1;
            Q1=sQuery(id+"F25.wireOp",EDGE,"E41");
            sweep(context, id + "F27", {"operationType" : NewBodyOperationType.ADD, "profiles" : qUnion([Q0]), "path" : qUnion([Q1])});
        }
        {
            var Q0;
            Q0=qCreatedBy(makeId("Front.planeOp"),FACE);
            var sketch = newSketch(context, id + "F28", { "sketchPlane" : qUnion([Q0])});
            skArc(sketch, "E44", {"start": v(0, 7.79) * mm, "mid": v(1, 8.79) * mm, "end": v(0, 9.79) * mm});
            skLineSegment(sketch, "E45", {"start": v(0, 9.79) * mm, "end": v(0, 7.79) * mm});
            skSolve(sketch);
        }
        {
            var Q0;
            Q0=qCreatedBy(makeId("Front.planeOp"),FACE);
            var sketch = newSketch(context, id + "F29", { "sketchPlane" : qUnion([Q0])});
            skLineSegment(sketch, "E46", {"start": v(0, 12.3) * mm, "end": v(0, 5.36) * mm, "construction": true});
            skSolve(sketch);
        }
        {
            var Q0;
            Q0=makeQuery(id+"F28.imprint","IMPRINT",FACE,{"disambiguationData":[TD([[makeQuery(id+"F28.imprint","IMPRINT",EDGE,{"derivedFrom":sQuery(id+"F28.wireOp",EDGE,"E44")}),1.0]])]});
            var Q1;
            Q1=sQuery(id+"F29.wireOp",EDGE,"E46");
            revolve(context, id + "F30", {"operationType" : NewBodyOperationType.REMOVE, "surfaceOperationType" : NewSurfaceOperationType.NEW, "entities" : qUnion([Q0]), "axis" : qUnion([Q1]), "revolveType" : RevolveType.FULL, "oppositeDirection" : true});
        }
        {
            var Q0;
            Q0=qCreatedBy(makeId("Front.planeOp"),FACE);
            var sketch = newSketch(context, id + "F31", { "sketchPlane" : qUnion([Q0])});
            skLineSegment(sketch, "E47", {"start": v(2.5, 0) * mm, "end": v(6.4, 5.6) * mm});
            skArc(sketch, "E48", {"start": v(2.5, 0) * mm, "mid": v(7.26, 0.84) * mm, "end": v(6.4, 5.6) * mm});
            skSolve(sketch);
        }
        {
            var Q0;
            Q0=makeQuery(id+"F31.imprint","IMPRINT",FACE,{"disambiguationData":[TD([[makeQuery(id+"F31.imprint","IMPRINT",EDGE,{"derivedFrom":sQuery(id+"F31.wireOp",EDGE,"E47")}),-1.0]])]});
            var Q1;
            Q1=sQuery(id+"F29.wireOp",EDGE,"E46");
            revolve(context, id + "F32", {"operationType" : NewBodyOperationType.REMOVE, "surfaceOperationType" : NewSurfaceOperationType.NEW, "entities" : qUnion([Q0]), "axis" : qUnion([Q1]), "revolveType" : RevolveType.FULL, "oppositeDirection" : true});
        }
        {
            var Q0;
            Q0=makeQuery(id+"F15.opExtrude","CAP_FACE",FACE,{"disambiguationData":[OSD([sQuery(id+"F14.wireOp",EDGE,"E34")])],"isStart":false});
            var sketch = newSketch(context, id + "F33", { "sketchPlane" : qUnion([Q0])});
            skCircle(sketch, "E49", {"center": v(0, 0) * mm, "radius": 6 * mm});
            skCircle(sketch, "E50", {"center": v(0, 0) * mm, "radius": 2.5 * mm});
            skSolve(sketch);
        }
        {
            var Q0;
            Q0 = qSketchRegion(id + "F33", true);
            extrude(context, id + "F34", {"entities" : qUnion([Q0]), "operationType" : NewBodyOperationType.ADD, "oppositeDirection" : true, "depth" : 5 * mm, "offsetDistance" : 25 * mm});
        }
        {
            var Q0;
            Q0=makeQuery(id+"F1.opRevolve","SWEPT_EDGE",EDGE,{"disambiguationData":[OSD([sQuery(id+"F0.wireOp",EDGE,"E1"),sQuery(id+"F0.wireOp",EDGE,"E2")])]});
            chamfer(context, id + "F35", {"entities" : qUnion([Q0]), "chamferType" : ChamferType.TWO_OFFSETS, "width1" : 0.4 * mm, "oppositeDirection" : false, "width2" : 18 * mm, "tangentPropagation" : true});
        }
        {
            var Q0;
            {var subQ0=sQuery(id+"F0.wireOp",EDGE,"E1");Q0=makeQuery(id+"F35.opChamfer","BLEND_EDGE",EDGE,{"blendedFrom":[makeQuery(id+"F1.opRevolve","SWEPT_EDGE",EDGE,{"disambiguationData":[OSD([subQ0,sQuery(id+"F0.wireOp",EDGE,"E2")])]}),makeQuery(id+"F1.opRevolve","SWEPT_FACE",FACE,{"disambiguationData":[OSD([subQ0])]})],"blendedInto":[makeQuery(id+"F1.opRevolve","SWEPT_FACE",FACE,{"disambiguationData":[OSD([subQ0])]})]});}
            fillet(context, id + "F36", {"entities" : qUnion([Q0]), "radius" : 0.2 * mm, "tangentPropagation" : true, "allowEdgeOverflow" : false});
        }
    });
